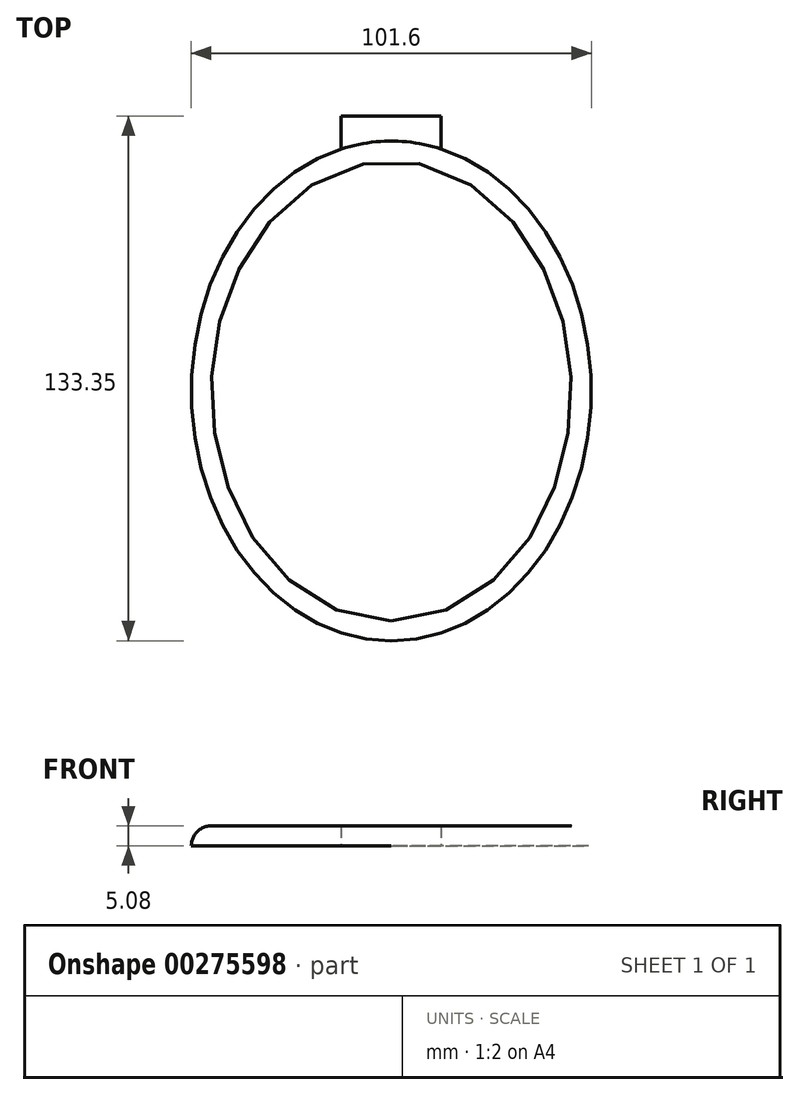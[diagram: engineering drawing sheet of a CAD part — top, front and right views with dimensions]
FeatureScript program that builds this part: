
annotation { "Feature Type Name" : "Feature", "Feature Type Description" : "" }
export const myFeature = defineFeature(function(context is Context, id is Id, definition is map)
    precondition{}
    {
        {
            var Q0;
            Q0=qCreatedBy(makeId("Top.planeOp"),FACE);
            var sketch = newSketch(context, id + "F0", { "sketchPlane" : qUnion([Q0])});
            skEllipse(sketch, "E0", {"center": v(0, 0) * mm, "majorRadius": 63.5 * mm, "minorRadius": 50.8 * mm, "majorAxis": v(0, -1)});
            skSolve(sketch);
        }
        {
            var Q0;
            Q0=makeQuery(id+"F0.imprint","IMPRINT",FACE,{"disambiguationData":[TD([[makeQuery(id+"F0.imprint","IMPRINT",EDGE,{"derivedFrom":sQuery(id+"F0.wireOp",EDGE,"E0")}),1.0]])]});
            extrude(context, id + "F1", {"entities" : qUnion([Q0]), "depth" : 5.08 * mm});
        }
        {
            var Q0;
            Q0=makeQuery(id+"F1.opExtrude","CAP_EDGE",EDGE,{"disambiguationData":[OSD([sQuery(id+"F0.wireOp",EDGE,"E0")])],"isStart":false});
            fillet(context, id + "F2", {"entities" : qUnion([Q0]), "radius" : 5.08 * mm, "tangentPropagation" : true, "allowEdgeOverflow" : false});
        }
        {
            var Q0;
            Q0=makeQuery(id+"F1.opExtrude","CAP_FACE",FACE,{"disambiguationData":[OSD([sQuery(id+"F0.wireOp",EDGE,"E0")])],"isStart":true});
            var sketch = newSketch(context, id + "F3", { "sketchPlane" : qUnion([Q0])});
            skLineSegment(sketch, "E1.bottom", {"start": v(-12.7, -57.15) * mm, "end": v(12.7, -57.15) * mm});
            skLineSegment(sketch, "E1.top", {"start": v(-12.7, -69.85) * mm, "end": v(12.7, -69.85) * mm});
            skLineSegment(sketch, "E1.left", {"start": v(-12.7, -57.15) * mm, "end": v(-12.7, -69.85) * mm});
            skLineSegment(sketch, "E1.right", {"start": v(12.7, -57.15) * mm, "end": v(12.7, -69.85) * mm});
            skPoint(sketch, "E1.middle", {"position": v(0, -63.5) * mm});
            skSolve(sketch);
        }
        {
            var Q0;
            {var subQ0=sQuery(id+"F3.wireOp",EDGE,"E1.top");Q0=makeQuery(id+"F3.imprint","IMPRINT",FACE,{"disambiguationData":[TD([[makeQuery(id+"F3.imprint","IMPRINT",EDGE,{"derivedFrom":subQ0}),1.0]])]});}
            extrude(context, id + "F4", {"entities" : qUnion([Q0]), "oppositeDirection" : true, "depth" : 5.08 * mm});
        }
    });
